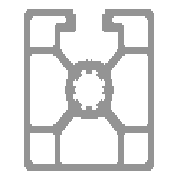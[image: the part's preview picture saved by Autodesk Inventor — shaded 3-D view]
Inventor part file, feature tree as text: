
AUTODESK INVENTOR PART (.ipt)
format: ipt  version: 2011 SP1 (Build 150282100, 282)  size: 389,632 bytes
history: native  units: mm
features: sketch x11, other x6, extrude x6, hole x2, plane x1
ambient origin geometry x8: Origin, YZ Plane, XZ Plane, XY Plane, X Axis, Y Axis, Z Axis, Center Point
bodies: Solid1 (feature_tree), Body (feature_tree)
feature tree (26):
  other  "45x45 1S"
  other  "Driven Length"
  other  "Blocks"
  other  "Start Plane"
  other  "End Plane"
  hole  "M12/-"  [1 undecoded]
  hole  "-/M12"  [1 undecoded]
  extrude  "D17/-"  Depth=10.0mm TaperAngle=0.0deg
  extrude  "-/D17"  Depth=22.5mm
  extrude  "D9.8/-"  Depth=9.8mm
  extrude  "-/D9.8"  Depth=10.0mm TaperAngle=0.0deg
  extrude  "-/D9.8VS"  Depth=22.5mm
  extrude  "D9.8VS/-"  Depth=9.8mm
  sketch  "Sketch1"  dims[d2=-0.0mm d3=25.0mm]
  sketch  "Sketch9"  dims[d4=0.13mm d5=0.0mm]
  sketch  "Sketch10"  dims[d17=10.106mm d18=6.0mm d19=4.0mm d20=2.0mm d21=90.0deg d22=55.0mm d23=20.594885mm]
  sketch  "Sketch11"  dims[d24=10.106mm d25=6.0mm d26=4.0mm d27=2.0mm d28=90.0deg d29=55.0mm d30=20.594885mm d31=22.5mm]
  sketch  "Sketch12"  dims[d32=17.0mm d33=10.0mm d34=0.0mm]
  sketch  "Sketch13"  dims[d35=17.0mm d36=22.5mm]
  sketch  "Sketch14"  dims[d37=10.0mm d38=0.0mm d39=9.8mm]
  sketch  "Sketch15"  dims[d40=22.5mm d41=10.0mm d42=0.0mm]
  sketch  "Sketch26"  dims[d43=9.8mm d44=22.5mm]
  sketch  "Sketch47"  dims[d45=10.0mm d46=0.0mm d47=9.8mm]
  plane  "Work Plane21"
  sketch  "Sketch48"  dims[d48=22.5mm d49=10.0mm d50=0.0mm d62=9.8mm d63=10.0mm d64=0.0mm d65=22.5mm d86=90.0deg d7=25.0mm]
  other  "45x45 1S:1"
note: 2 required parameter values undecoded (feature->parameter linkage not recoverable at this tier; creation-order binding heuristic only, values carry confidence <= 0.55)
